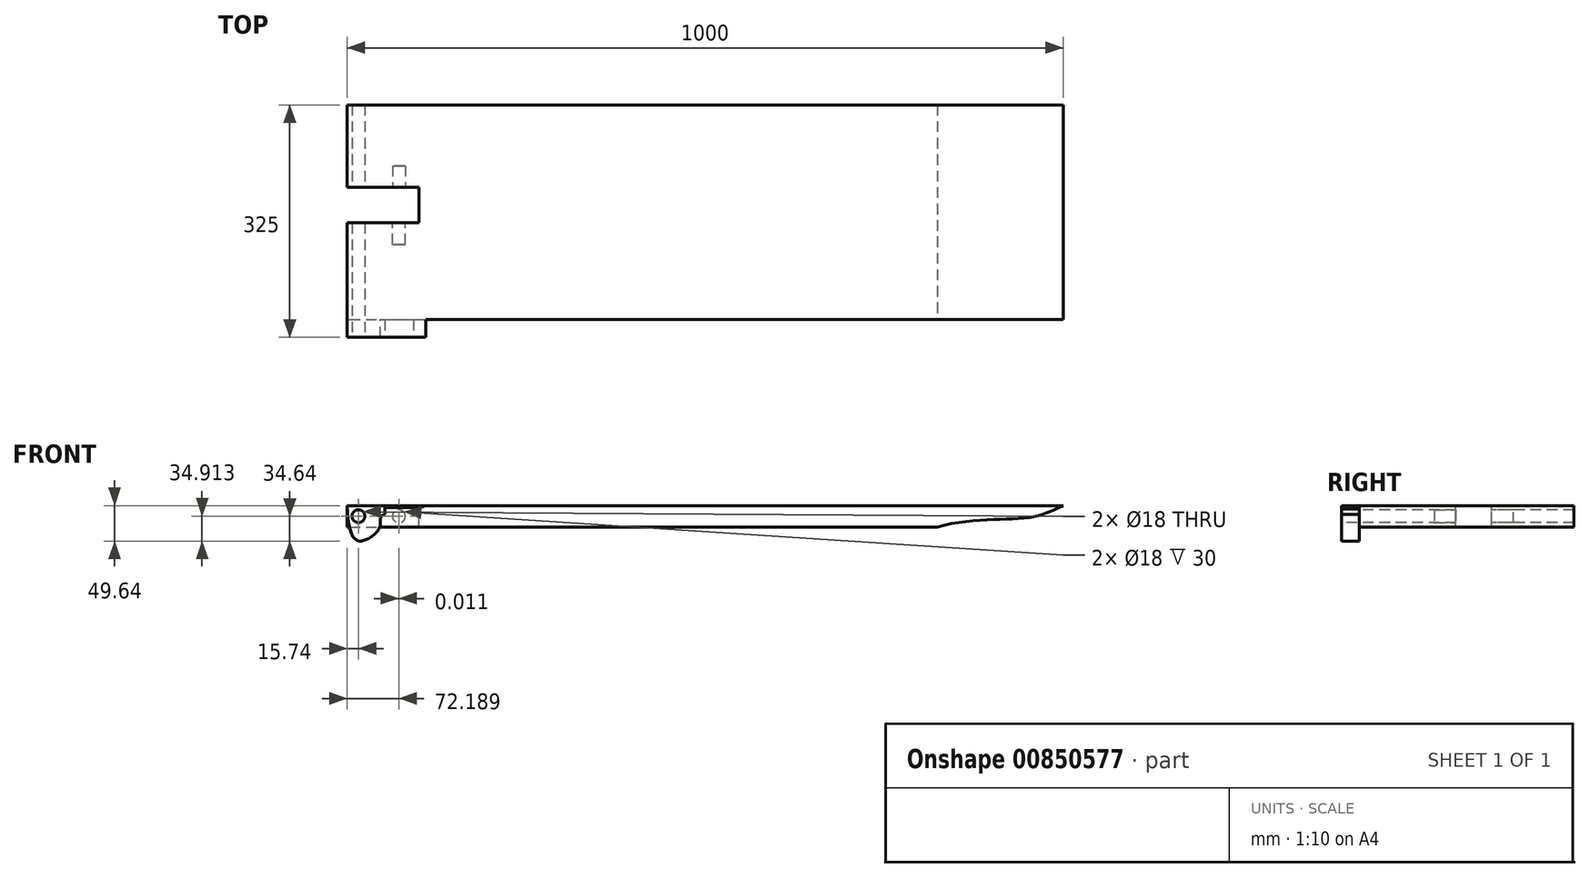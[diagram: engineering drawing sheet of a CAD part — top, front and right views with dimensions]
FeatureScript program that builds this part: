
annotation { "Feature Type Name" : "Feature", "Feature Type Description" : "" }
export const myFeature = defineFeature(function(context is Context, id is Id, definition is map)
    precondition{}
    {
        {
            var Q0;
            Q0=qCreatedBy(makeId("Top.planeOp"),FACE);
            var sketch = newSketch(context, id + "F0", { "sketchPlane" : qUnion([Q0])});
            skLineSegment(sketch, "E0.bottom", {"start": v(-460, 150) * mm, "end": v(540, 150) * mm});
            skLineSegment(sketch, "E0.top", {"start": v(-460, -150) * mm, "end": v(540, -150) * mm});
            skLineSegment(sketch, "E0.left", {"start": v(-460, 150) * mm, "end": v(-460, -150) * mm});
            skLineSegment(sketch, "E0.right", {"start": v(540, 150) * mm, "end": v(540, -150) * mm});
            skSolve(sketch);
        }
        {
            var Q0;
            Q0 = qSketchRegion(id + "F0", true);
            extrude(context, id + "F1", {"entities" : qUnion([Q0]), "depth" : 30 * mm, "offsetDistance" : 25 * mm});
        }
        {
            var Q0;
            Q0=makeQuery(id+"F1.opExtrude","SWEPT_FACE",FACE,{"disambiguationData":[OSD([sQuery(id+"F0.wireOp",EDGE,"E0.top")])]});
            var sketch = newSketch(context, id + "F2", { "sketchPlane" : qUnion([Q0])});
            skPoint(sketch, "E1.3.internal.snap0", {"position": v(-460, 15) * mm});
            skFitSpline(sketch, "E1", {"points": [v(-460, 30) * mm, v(-442.54, -19.6) * mm, v(-414.45, 0) * mm, v(-411.98, 15) * mm, v(-350, 30) * mm], "startDerivative": vector(18.9, -308.1) * mm, "endDerivative": vector(216.28, 83.2) * mm});
            skFitSpline(sketch, "E2", {"points": [v(363.85, 0) * mm, v(494.07, 13.64) * mm, v(540, 30) * mm], "startDerivative": vector(230.29, 66.9) * mm, "endDerivative": vector(104.43, 47.2) * mm});
            skSolve(sketch);
        }
        {
            var Q0;
            Q0 = qSketchRegion(id + "F2", true);
            var Q1;
            {var subQ0=sQuery(id+"F2.wireOp",EDGE,"E1");var subQ1=makeQuery(id+"F1.opExtrude","CAP_EDGE",EDGE,{"disambiguationData":[OSD([sQuery(id+"F0.wireOp",EDGE,"E0.top")])],"isStart":true});var subQ2=makeQuery(id+"F2.imprint","INTERSECT",VERTEX,{"disambiguationData":[OD(0.0)],"derivedFrom":[subQ1,subQ0]});Q1=makeQuery(id+"F2.imprint","IMPRINT",FACE,{"disambiguationData":[TD([[makeQuery(id+"F2.imprint","IMPRINT",EDGE,{"disambiguationData":[TD([[subQ2,-1.0]])],"derivedFrom":subQ0}),1.0]])]});}
            var Q2;
            {var subQ0=sQuery(id+"F2.wireOp",EDGE,"E1");var subQ1=sQuery(id+"F0.wireOp",EDGE,"E0.top");var subQ2=makeQuery(id+"F1.opExtrude","CAP_EDGE",EDGE,{"disambiguationData":[OSD([subQ1])],"isStart":false});var subQ6=makeQuery(id+"F2.imprint","INTERSECT",VERTEX,{"derivedFrom":[subQ2,subQ0]});Q2=makeQuery(id+"F2.imprint","IMPRINT",FACE,{"disambiguationData":[TD([[makeQuery(id+"F2.imprint","IMPRINT",EDGE,{"disambiguationData":[TD([[subQ6,1.0]])],"derivedFrom":subQ0}),1.0]])]});}
            extrude(context, id + "F3", {"entities" : qUnion([Q0, Q1, Q2]), "operationType" : NewBodyOperationType.ADD, "depth" : 25 * mm, "offsetDistance" : 25 * mm});
        }
        {
            var Q0;
            Q0=makeQuery(id+"F3.opExtrude","CAP_FACE",FACE,{"disambiguationData":[OSD([sQuery(id+"F0.wireOp",EDGE,"E0.top"),sQuery(id+"F2.wireOp",EDGE,"E1")])],"isStart":false});
            var sketch = newSketch(context, id + "F4", { "sketchPlane" : qUnion([Q0])});
            skCircle(sketch, "E3", {"center": v(-439.73, 17.91) * mm, "radius": 5 * mm});
            skSolve(sketch);
        }
        {
            var Q0;
            Q0 = qSketchRegion(id + "F4", true);
            extrude(context, id + "F5", {"entities" : qUnion([Q0]), "operationType" : NewBodyOperationType.ADD, "oppositeDirection" : true, "depth" : 25 * mm, "offsetDistance" : 25 * mm});
        }
        {
            var Q0;
            Q0=makeQuery(id+"F3.opExtrude","CAP_FACE",FACE,{"disambiguationData":[OSD([sQuery(id+"F0.wireOp",EDGE,"E0.top"),sQuery(id+"F2.wireOp",EDGE,"E1")])],"isStart":false});
            var sketch = newSketch(context, id + "F6", { "sketchPlane" : qUnion([Q0])});
            skCircle(sketch, "E4", {"center": v(-444.26, 15.27) * mm, "radius": 9 * mm});
            skLineSegment(sketch, "E5", {"start": v(-407.09, 17.82) * mm, "end": v(-407.09, 27.47) * mm});
            skLineSegment(sketch, "E6", {"start": v(-407.09, 27.47) * mm, "end": v(-367.09, 27.47) * mm});
            skLineSegment(sketch, "E7", {"start": v(-367.09, 27.47) * mm, "end": v(-367.09, 25.2) * mm});
            skSolve(sketch);
        }
        {
            var Q0;
            Q0=makeQuery(id+"F6.imprint","IMPRINT",FACE,{"disambiguationData":[TD([[makeQuery(id+"F6.imprint","IMPRINT",EDGE,{"derivedFrom":sQuery(id+"F6.wireOp",EDGE,"E4")}),1.0]])]});
            extrude(context, id + "F7", {"entities" : qUnion([Q0]), "operationType" : NewBodyOperationType.REMOVE, "oppositeDirection" : true, "depth" : 800 * mm, "offsetDistance" : 25 * mm});
        }
        {
            var Q0;
            {var subQ0=sQuery(id+"F0.wireOp",EDGE,"E0.top");Q0=makeQuery(id+"FDAGC5iYNOmhHux_1.1.F3.boolean.opBoolean","MERGE",FACE,{"derivedFrom":[makeQuery(id+"F3.boolean.opBoolean","MERGE",FACE,{"derivedFrom":[makeQuery(id+"F1.opExtrude","CAP_FACE",FACE,{"disambiguationData":[OSD([sQuery(id+"F0.wireOp",EDGE,"E0.bottom"),subQ0,sQuery(id+"F0.wireOp",EDGE,"E0.left"),sQuery(id+"F0.wireOp",EDGE,"E0.right")])],"isStart":false}),makeQuery(id+"F3.opExtrude","SWEPT_FACE",FACE,{"disambiguationData":[OSD([subQ0])]})]}),makeQuery(id+"FDAGC5iYNOmhHux_1.1.F3.opExtrude","SWEPT_FACE",FACE,{"disambiguationData":[OSD([subQ0])]})]});}
            var sketch = newSketch(context, id + "F8", { "sketchPlane" : qUnion([Q0])});
            skLineSegment(sketch, "E8.bottom", {"start": v(-460, 35) * mm, "end": v(-360, 35) * mm});
            skLineSegment(sketch, "E8.top", {"start": v(-460, -15) * mm, "end": v(-360, -15) * mm});
            skLineSegment(sketch, "E8.left", {"start": v(-460, 35) * mm, "end": v(-460, -15) * mm});
            skLineSegment(sketch, "E8.right", {"start": v(-360, 35) * mm, "end": v(-360, -15) * mm});
            skSolve(sketch);
        }
        {
            var Q0;
            Q0 = qSketchRegion(id + "F8", true);
            extrude(context, id + "F9", {"entities" : qUnion([Q0]), "operationType" : NewBodyOperationType.REMOVE, "oppositeDirection" : true, "depth" : 50 * mm, "offsetDistance" : 25 * mm});
        }
        {
            var Q0;
            Q0=makeQuery(id+"F9.boolean.opBoolean","COPY",FACE,{"derivedFrom":makeQuery(id+"F9.opExtrude","SWEPT_FACE",FACE,{"disambiguationData":[OSD([sQuery(id+"F8.wireOp",EDGE,"E8.bottom")])]})});
            var sketch = newSketch(context, id + "F10", { "sketchPlane" : qUnion([Q0])});
            skPoint(sketch, "E9.startSnap0", {"position": v(-410, 30) * mm});
            skPoint(sketch, "E9.endSnap0", {"position": v(-410, 0) * mm});
            skCircle(sketch, "E10", {"center": v(-387.8, 15) * mm, "radius": 9 * mm});
            skSolve(sketch);
        }
        {
            var Q0;
            Q0 = qSketchRegion(id + "F10", true);
            extrude(context, id + "F11", {"entities" : qUnion([Q0]), "operationType" : NewBodyOperationType.REMOVE, "oppositeDirection" : true, "depth" : 30 * mm, "offsetDistance" : 25 * mm});
        }
        {
            var Q0;
            Q0=makeQuery(id+"F9.boolean.opBoolean","COPY",FACE,{"derivedFrom":makeQuery(id+"F9.opExtrude","SWEPT_FACE",FACE,{"disambiguationData":[OSD([sQuery(id+"F8.wireOp",EDGE,"E8.top")])]})});
            var sketch = newSketch(context, id + "F12", { "sketchPlane" : qUnion([Q0])});
            skCircle(sketch, "E11", {"center": v(387.81, 15) * mm, "radius": 9 * mm});
            skSolve(sketch);
        }
        {
            var Q0;
            Q0 = qSketchRegion(id + "F12", true);
            extrude(context, id + "F13", {"entities" : qUnion([Q0]), "operationType" : NewBodyOperationType.REMOVE, "oppositeDirection" : true, "depth" : 30 * mm, "offsetDistance" : 25 * mm});
        }
        {
            var Q0;
            {var subQ0=sQuery(id+"F6.wireOp",EDGE,"E5");Q0=makeQuery(id+"F6.imprint","IMPRINT",FACE,{"disambiguationData":[TD([[makeQuery(id+"F6.imprint","IMPRINT",EDGE,{"derivedFrom":subQ0}),-1.0]])]});}
            extrude(context, id + "F14", {"entities" : qUnion([Q0]), "operationType" : NewBodyOperationType.REMOVE, "oppositeDirection" : true, "depth" : 25 * mm, "offsetDistance" : 25 * mm});
        }
        {
            var Q0;
            {var subQ0=sQuery(id+"F2.wireOp",EDGE,"E2");Q0=makeQuery(id+"F2.imprint","IMPRINT",FACE,{"disambiguationData":[TD([[makeQuery(id+"F2.imprint","IMPRINT",EDGE,{"derivedFrom":subQ0}),-1.0]])]});}
            extrude(context, id + "F15", {"entities" : qUnion([Q0]), "operationType" : NewBodyOperationType.REMOVE, "oppositeDirection" : true, "depth" : 300 * mm, "offsetDistance" : 25 * mm});
        }
    });
